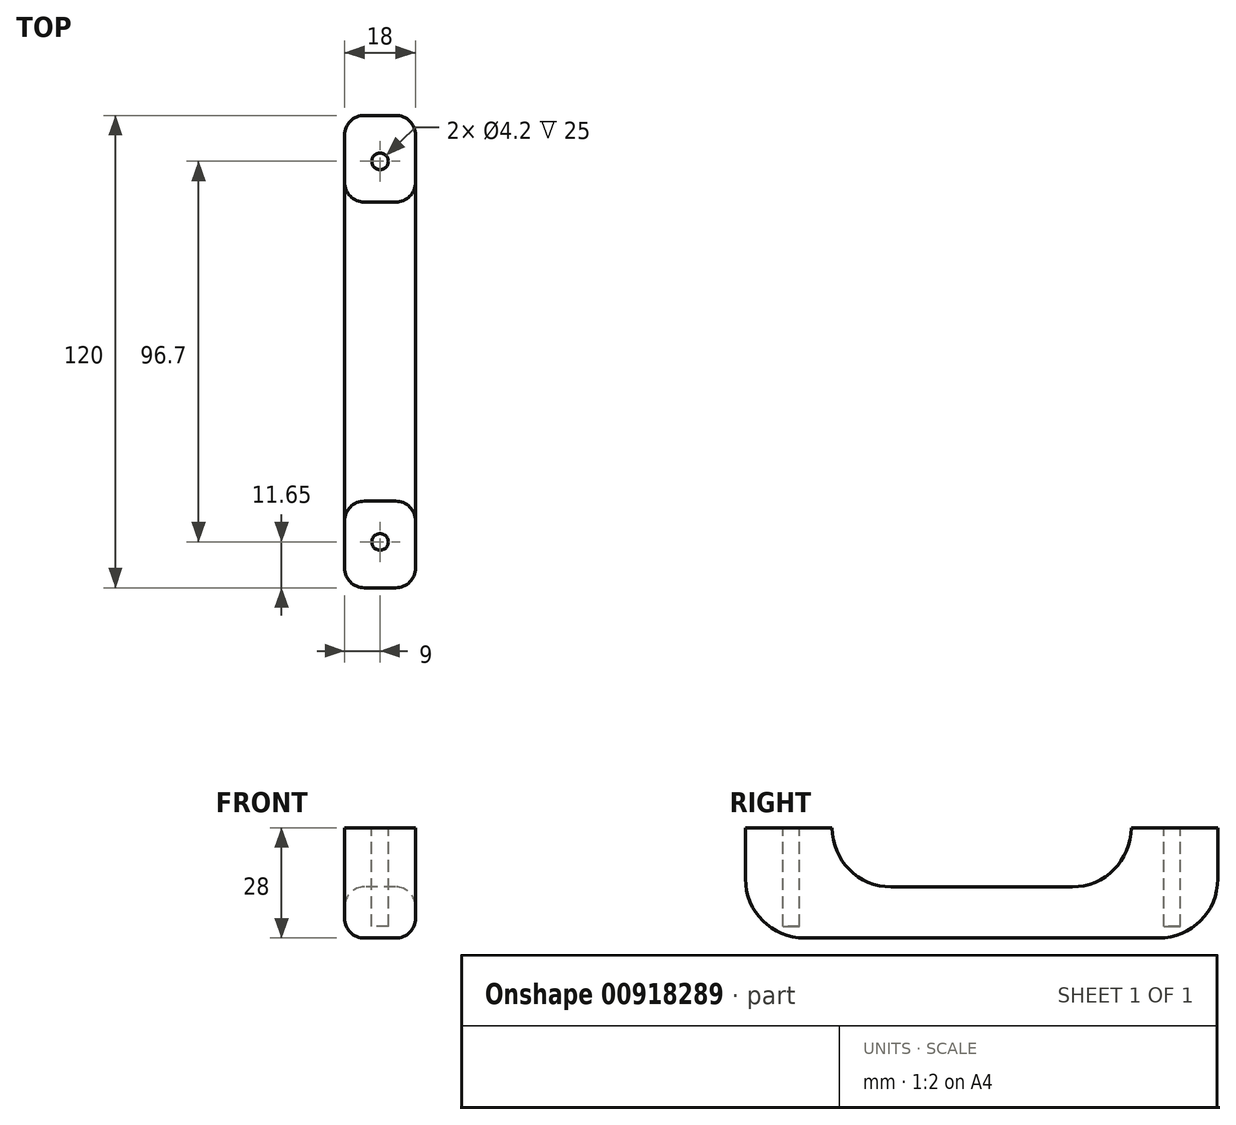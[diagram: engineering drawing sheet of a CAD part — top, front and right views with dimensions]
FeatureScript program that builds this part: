
annotation { "Feature Type Name" : "Feature", "Feature Type Description" : "" }
export const myFeature = defineFeature(function(context is Context, id is Id, definition is map)
    precondition{}
    {
        {
            var Q0;
            Q0=qCreatedBy(makeId("Right.planeOp"),FACE);
            var sketch = newSketch(context, id + "F0", { "sketchPlane" : qUnion([Q0])});
            skLineSegment(sketch, "E0", {"start": v(-60, 0) * mm, "end": v(0, 0) * mm});
            skLineSegment(sketch, "E1", {"start": v(0, 0) * mm, "end": v(60, 0) * mm});
            skLineSegment(sketch, "E2", {"start": v(-60, 0) * mm, "end": v(-60, 28) * mm});
            skLineSegment(sketch, "E3", {"start": v(-60, 28) * mm, "end": v(-38, 28) * mm});
            skLineSegment(sketch, "E4", {"start": v(-38, 28) * mm, "end": v(-38, 13) * mm});
            skLineSegment(sketch, "E5", {"start": v(-38, 13) * mm, "end": v(38, 13) * mm});
            skLineSegment(sketch, "E6", {"start": v(38, 13) * mm, "end": v(38, 28) * mm});
            skLineSegment(sketch, "E7", {"start": v(38, 28) * mm, "end": v(60, 28) * mm});
            skLineSegment(sketch, "E8", {"start": v(60, 28) * mm, "end": v(60, 0) * mm});
            skSolve(sketch);
        }
        {
            var Q0;
            Q0=makeQuery(id+"F0.imprint","IMPRINT",FACE,{"disambiguationData":[TD([[makeQuery(id+"F0.imprint","IMPRINT",EDGE,{"derivedFrom":sQuery(id+"F0.wireOp",EDGE,"E0")}),1.0]])]});
            extrude(context, id + "F1", {"entities" : qUnion([Q0]), "depth" : 18 * mm, "offsetDistance" : 25 * mm});
        }
        {
            var Q0;
            Q0=qCreatedBy(makeId("Top.planeOp"),FACE);
            var Q1;
            Q1 = qBodyType(qCreatedBy(id + "FELylvt7RjJouEV_1" ,EDGE), BodyType.WIRE);
            cPlane(context, id + "F2", {"entities" : qUnion([Q0, Q1]), "cplaneType" : CPlaneType.OFFSET, "offset" : 28 * mm, "width" : 150 * mm, "height" : 150 * mm});
        }
        {
            var Q0;
            Q0=qCreatedBy(id+"F2.planeOp",FACE);
            var sketch = newSketch(context, id + "F3", { "sketchPlane" : qUnion([Q0])});
            skCircle(sketch, "E9", {"center": v(9, 48.35) * mm, "radius": 2.1 * mm});
            skCircle(sketch, "E10", {"center": v(9, -48.35) * mm, "radius": 2.1 * mm});
            skSolve(sketch);
        }
        {
            var Q0;
            Q0=makeQuery(id+"F3.imprint","IMPRINT",FACE,{"disambiguationData":[TD([[makeQuery(id+"F3.imprint","IMPRINT",EDGE,{"derivedFrom":sQuery(id+"F3.wireOp",EDGE,"E9")}),1.0]])]});
            var Q1;
            Q1=makeQuery(id+"F3.imprint","IMPRINT",FACE,{"disambiguationData":[TD([[makeQuery(id+"F3.imprint","IMPRINT",EDGE,{"derivedFrom":sQuery(id+"F3.wireOp",EDGE,"E10")}),1.0]])]});
            extrude(context, id + "F4", {"entities" : qUnion([Q0, Q1]), "operationType" : NewBodyOperationType.REMOVE, "oppositeDirection" : true, "depth" : 25 * mm, "offsetDistance" : 25 * mm});
        }
        {
            var Q0;
            Q0=makeQuery(id+"F1.opExtrude","SWEPT_EDGE",EDGE,{"disambiguationData":[OSD([sQuery(id+"F0.wireOp",EDGE,"E1"),sQuery(id+"F0.wireOp",EDGE,"E8")])]});
            var Q1;
            Q1=makeQuery(id+"F1.opExtrude","SWEPT_EDGE",EDGE,{"disambiguationData":[OSD([sQuery(id+"F0.wireOp",EDGE,"E0"),sQuery(id+"F0.wireOp",EDGE,"E2")])]});
            var Q2;
            Q2=makeQuery(id+"F1.opExtrude","SWEPT_EDGE",EDGE,{"disambiguationData":[OSD([sQuery(id+"F0.wireOp",EDGE,"E4"),sQuery(id+"F0.wireOp",EDGE,"E5")])]});
            var Q3;
            Q3=makeQuery(id+"F1.opExtrude","SWEPT_EDGE",EDGE,{"disambiguationData":[OSD([sQuery(id+"F0.wireOp",EDGE,"E5"),sQuery(id+"F0.wireOp",EDGE,"E6")])]});
            fillet(context, id + "F5", {"entities" : qUnion([Q0, Q1, Q2, Q3]), "radius" : 15 * mm, "tangentPropagation" : true, "allowEdgeOverflow" : false});
        }
        {
            var Q0;
            Q0=makeQuery(id+"F1.opExtrude","CAP_EDGE",EDGE,{"disambiguationData":[OSD([sQuery(id+"F0.wireOp",EDGE,"E0"),sQuery(id+"F0.wireOp",EDGE,"E1")])],"isStart":true});
            var Q1;
            Q1=makeQuery(id+"F1.opExtrude","CAP_EDGE",EDGE,{"disambiguationData":[OSD([sQuery(id+"F0.wireOp",EDGE,"E0"),sQuery(id+"F0.wireOp",EDGE,"E1")])],"isStart":false});
            var Q2;
            Q2=makeQuery(id+"F1.opExtrude","CAP_EDGE",EDGE,{"disambiguationData":[OSD([sQuery(id+"F0.wireOp",EDGE,"E5")])],"isStart":true});
            var Q3;
            Q3=makeQuery(id+"F1.opExtrude","CAP_EDGE",EDGE,{"disambiguationData":[OSD([sQuery(id+"F0.wireOp",EDGE,"E5")])],"isStart":false});
            fillet(context, id + "F6", {"entities" : qUnion([Q0, Q1, Q2, Q3]), "radius" : 5 * mm, "tangentPropagation" : true, "allowEdgeOverflow" : false});
        }
    });
